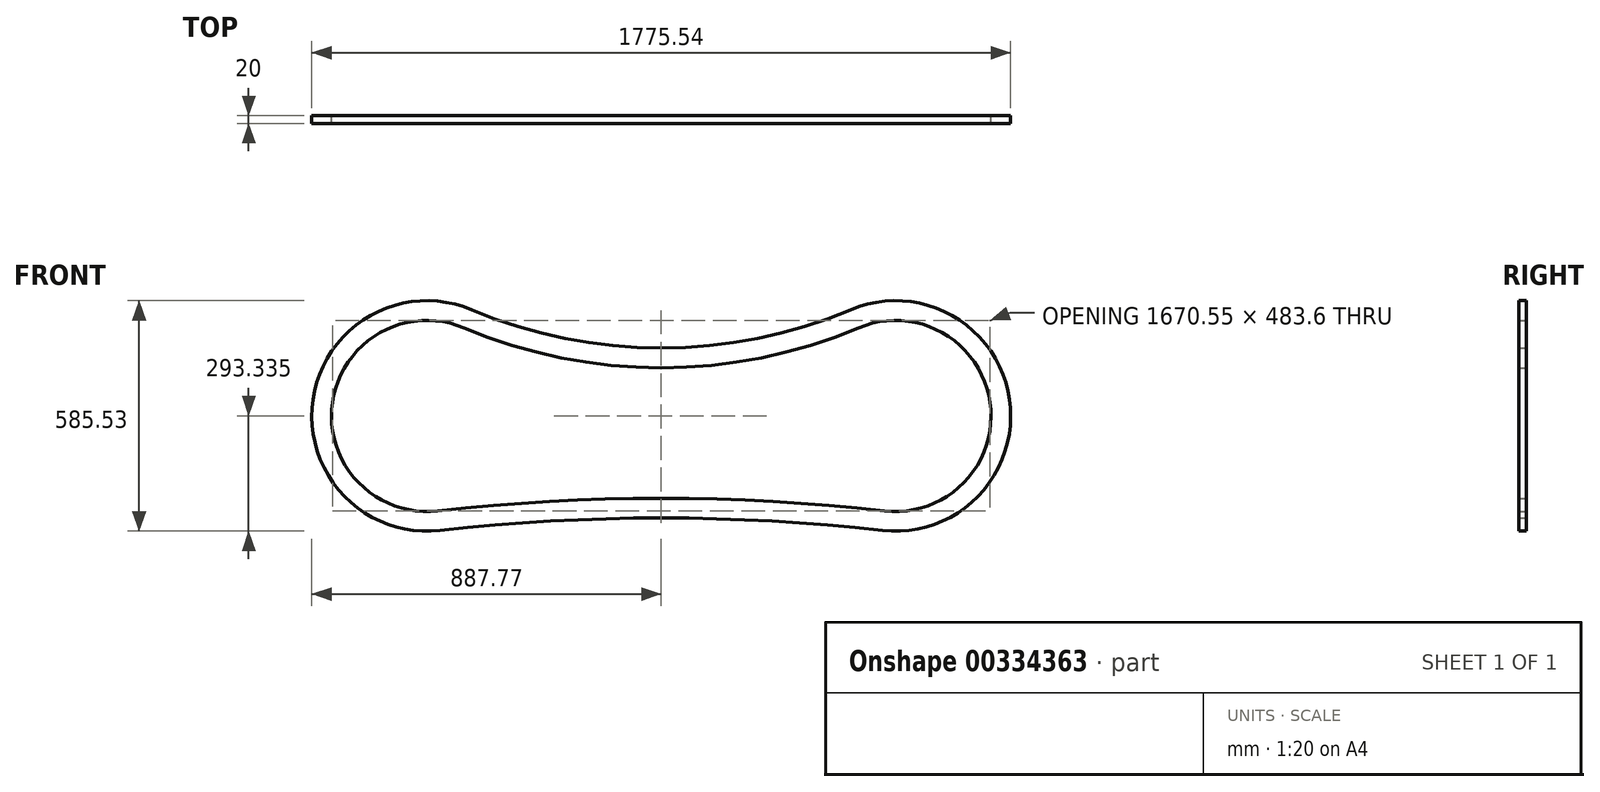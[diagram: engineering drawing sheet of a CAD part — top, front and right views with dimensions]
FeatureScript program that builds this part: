
annotation { "Feature Type Name" : "Feature", "Feature Type Description" : "" }
export const myFeature = defineFeature(function(context is Context, id is Id, definition is map)
    precondition{}
    {
        {
            var Q0;
            Q0=qCreatedBy(makeId("Front.planeOp"),FACE);
            var sketch = newSketch(context, id + "F0", { "sketchPlane" : qUnion([Q0])});
            skArc(sketch, "E0", {"start": v(-563.38, 296.99) * mm, "mid": v(-967, 69.1) * mm, "end": v(-644.32, -263.65) * mm});
            skArc(sketch, "E1", {"start": v(479.86, -263.65) * mm, "mid": v(802.53, 69.1) * mm, "end": v(398.92, 296.99) * mm});
            skLineSegment(sketch, "E2", {"start": v(-677.23, 27.26) * mm, "end": v(512.77, 27.26) * mm});
            skArc(sketch, "E3", {"start": v(479.86, -263.65) * mm, "mid": v(-82.23, -231.95) * mm, "end": v(-644.32, -263.65) * mm});
            skPoint(sketch, "E3.centerSnap0", {"position": v(-82.23, 27.26) * mm});
            skArc(sketch, "E4", {"start": v(-563.38, 296.99) * mm, "mid": v(-82.23, 199.6) * mm, "end": v(398.92, 296.99) * mm});
            skArc(sketch, "E5.0", {"start": v(-582.82, 250.92) * mm, "mid": v(-917.5, 61.95) * mm, "end": v(-649.94, -213.96) * mm});
            skArc(sketch, "E5.1", {"start": v(-582.82, 250.92) * mm, "mid": v(-82.23, 149.6) * mm, "end": v(418.36, 250.92) * mm});
            skArc(sketch, "E5.2", {"start": v(485.48, -213.96) * mm, "mid": v(753.05, 61.95) * mm, "end": v(418.36, 250.92) * mm});
            skArc(sketch, "E5.3", {"start": v(485.48, -213.96) * mm, "mid": v(-82.23, -181.95) * mm, "end": v(-649.94, -213.96) * mm});
            skSolve(sketch);
        }
        {
            var Q0;
            Q0=makeQuery(id+"F0.imprint","IMPRINT",FACE,{"disambiguationData":[TD([[makeQuery(id+"F0.imprint","IMPRINT",EDGE,{"derivedFrom":sQuery(id+"F0.wireOp",EDGE,"E0")}),1.0]])]});
            extrude(context, id + "F1", {"entities" : qUnion([Q0]), "depth" : 20 * mm});
        }
    });
